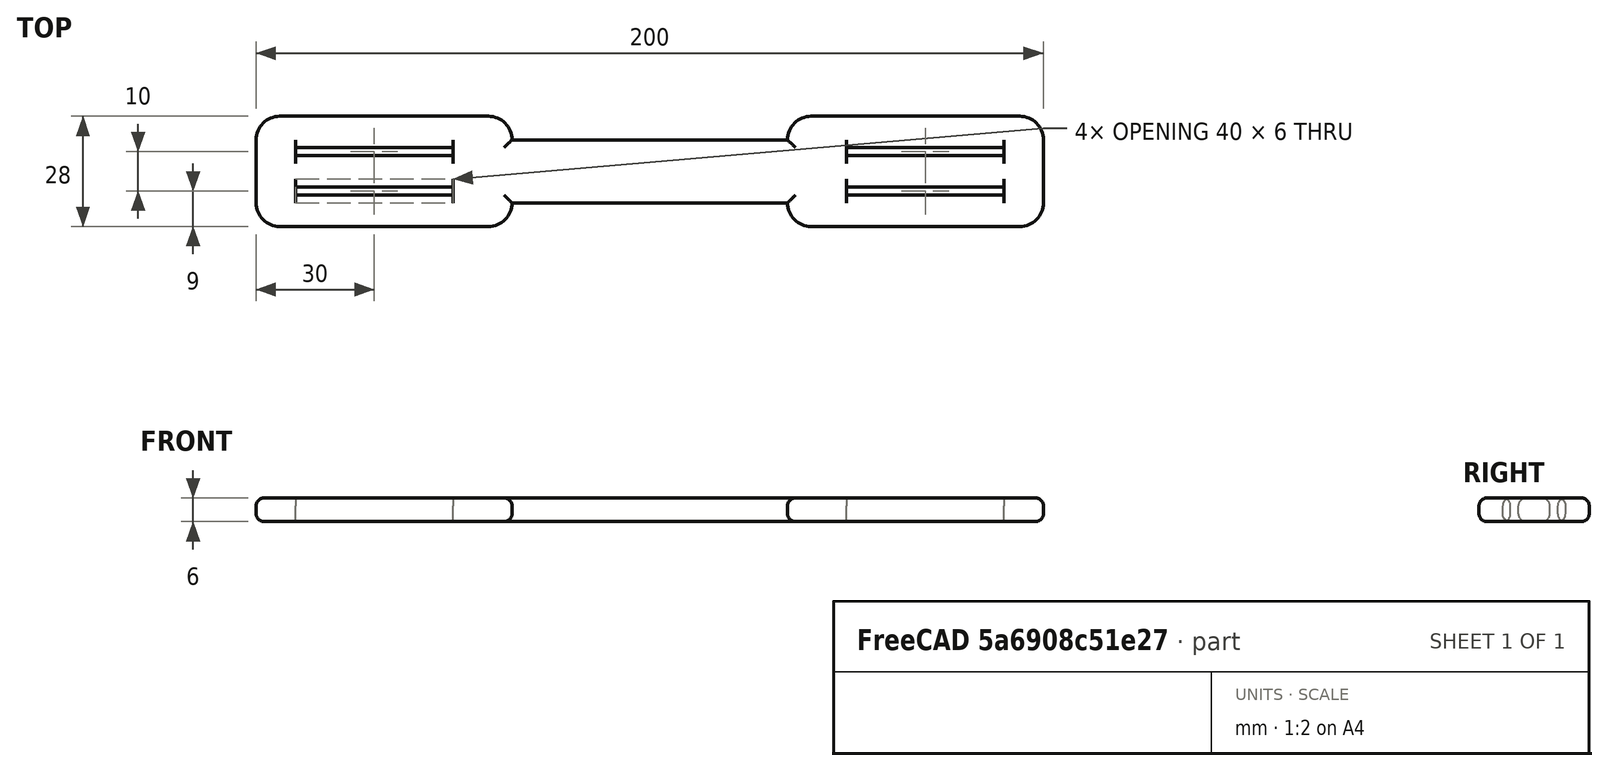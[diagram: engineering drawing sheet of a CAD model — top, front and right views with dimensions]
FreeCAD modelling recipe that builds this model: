
FCSTD DOCUMENT  (FreeCAD 0.18R4 (GitTag))
Label: Buckle Long 4_4
License: All rights reserved
LicenseURL: http://en.wikipedia.org/wiki/All_rights_reserved
objects: Part::Box×7, Part::Fillet×2, Part::MultiFuse×1, Part::Cut×1
note: 11 computed .brp shape members not serialized (recipe doc carries the construction recipe); baked Part::Feature solids carry a one-line shape summary decoded from their .brp

FEATURE [Part::Box] Box  label="Cube"
  AttacherType = Attacher::AttachEngine3D
  Height = 6
  Length = 200
  Placement = pos=(-110,-14,0) rot=(0,0,1;0rad)
  Width = 28
FEATURE [Part::Box] Box001  label="Cube001"
  AttacherType = Attacher::AttachEngine3D
  Height = 10
  Length = 40
  Placement = pos=(-100,-6,0) rot=(0,0,1;0rad)
  Width = 2
FEATURE [Part::Box] Box002  label="Cube002"
  AttacherType = Attacher::AttachEngine3D
  Height = 10
  Length = 40
  Placement = pos=(-100,4,0) rot=(0,0,1;0rad)
  Width = 2
FEATURE [Part::Box] Box003  label="Cube003"
  AttacherType = Attacher::AttachEngine3D
  Height = 10
  Length = 40
  Placement = pos=(40,-6,0) rot=(0,0,1;0rad)
  Width = 2
FEATURE [Part::Box] Box004  label="Cube004"
  AttacherType = Attacher::AttachEngine3D
  Height = 10
  Length = 40
  Placement = pos=(40,4,0) rot=(0,0,1;0rad)
  Width = 2
FEATURE [Part::Box] Box005  label="Cube005"
  AttacherType = Attacher::AttachEngine3D
  Height = 10
  Length = 70
  Placement = pos=(-45,-14,0) rot=(0,0,1;0rad)
  Width = 6
FEATURE [Part::Box] Box006  label="Cube006"
  AttacherType = Attacher::AttachEngine3D
  Height = 10
  Length = 70
  Placement = pos=(-45,8,0) rot=(0,0,1;0rad)
  Width = 6
FEATURE [Part::MultiFuse] Fusion  label="Holes"
  Refine = true
  Shapes = -> [Box001,Box003,Box004,Box002,Box005,Box006]
FEATURE [Part::Cut] Cut  label="Base"
  Base = -> Box
  Refine = true
  Tool = -> Fusion
FEATURE [Part::Fillet] Fillet
  Base = -> Cut
  Edges = 8 edges r=5.99: [Edge1,Edge3,Edge6,Edge35,Edge64,Edge65,Edge66,Edge67]
FEATURE [Part::Fillet] Fillet001
  Base = -> Fillet
  Edges = 48 edges r=2: [Edge1,Edge4,Edge5,Edge6,Edge7,Edge9,Edge10,Edge11,Edge13,Edge14,Edge16,Edge17,Edge18,Edge20,Edge21,Edge22,Edge23,Edge24,Edge26,Edge28,Edge30,Edge32,Edge34,Edge36,Edge38,Edge40,Edge42,Edge44,Edge45,Edge47,Edge48,Edge50,Edge51,Edge53,Edge54,Edge55,Edge57,Edge58,Edge59,Edge60,Edge62,Edge64,Edge66,+5 more]
